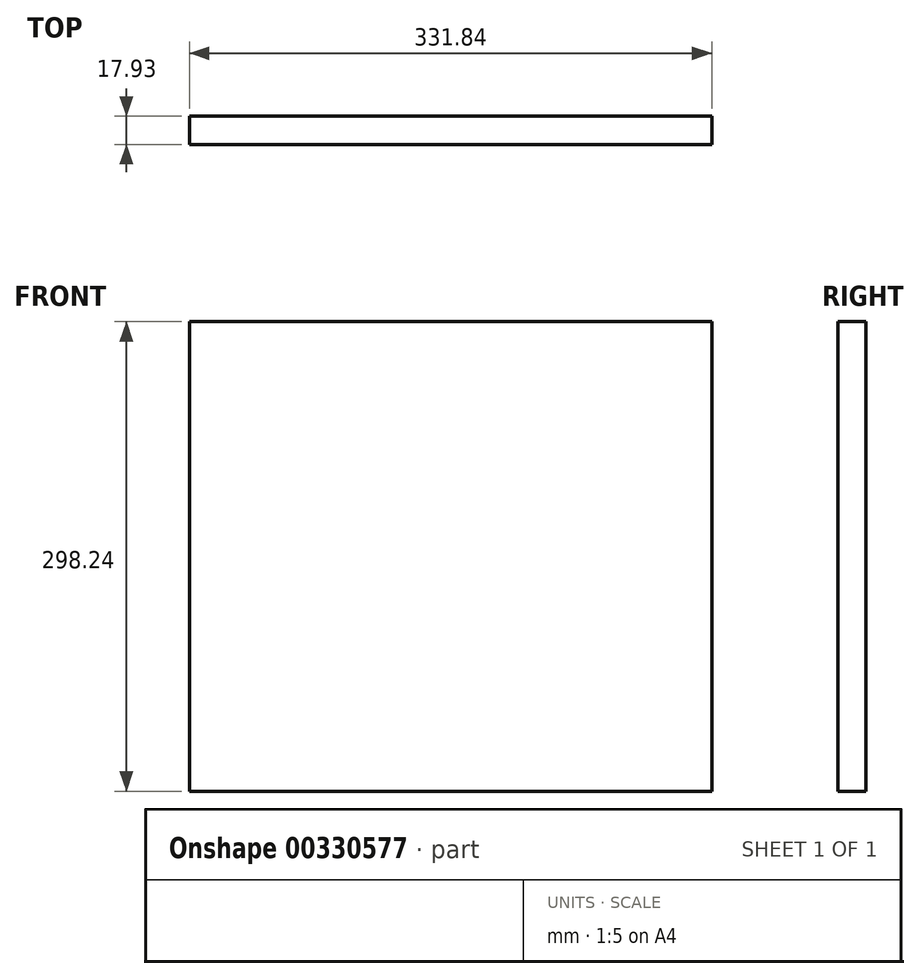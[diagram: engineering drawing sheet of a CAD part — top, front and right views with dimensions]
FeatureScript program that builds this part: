
annotation { "Feature Type Name" : "Feature", "Feature Type Description" : "" }
export const myFeature = defineFeature(function(context is Context, id is Id, definition is map)
    precondition{}
    {
        {
            var Q0;
            Q0=qCreatedBy(makeId("Front.planeOp"),FACE);
            var sketch = newSketch(context, id + "F0", { "sketchPlane" : qUnion([Q0])});
            skLineSegment(sketch, "E0.bottom", {"start": v(-167.62, -158.82) * mm, "end": v(164.22, -158.82) * mm});
            skLineSegment(sketch, "E0.top", {"start": v(-167.62, 139.42) * mm, "end": v(164.22, 139.42) * mm});
            skLineSegment(sketch, "E0.left", {"start": v(-167.62, -158.82) * mm, "end": v(-167.62, 139.42) * mm});
            skLineSegment(sketch, "E0.right", {"start": v(164.22, -158.82) * mm, "end": v(164.22, 139.42) * mm});
            skPoint(sketch, "E0.middle", {"position": v(-1.7, -9.7) * mm});
            skSolve(sketch);
        }
        {
            var Q0;
            Q0=makeQuery(id+"F0.imprint","IMPRINT",FACE,{"disambiguationData":[TD([[makeQuery(id+"F0.imprint","IMPRINT",EDGE,{"derivedFrom":sQuery(id+"F0.wireOp",EDGE,"E0.bottom")}),1.0]])]});
            extrude(context, id + "F1", {"entities" : qUnion([Q0]), "depth" : 17.93 * mm});
        }
    });
